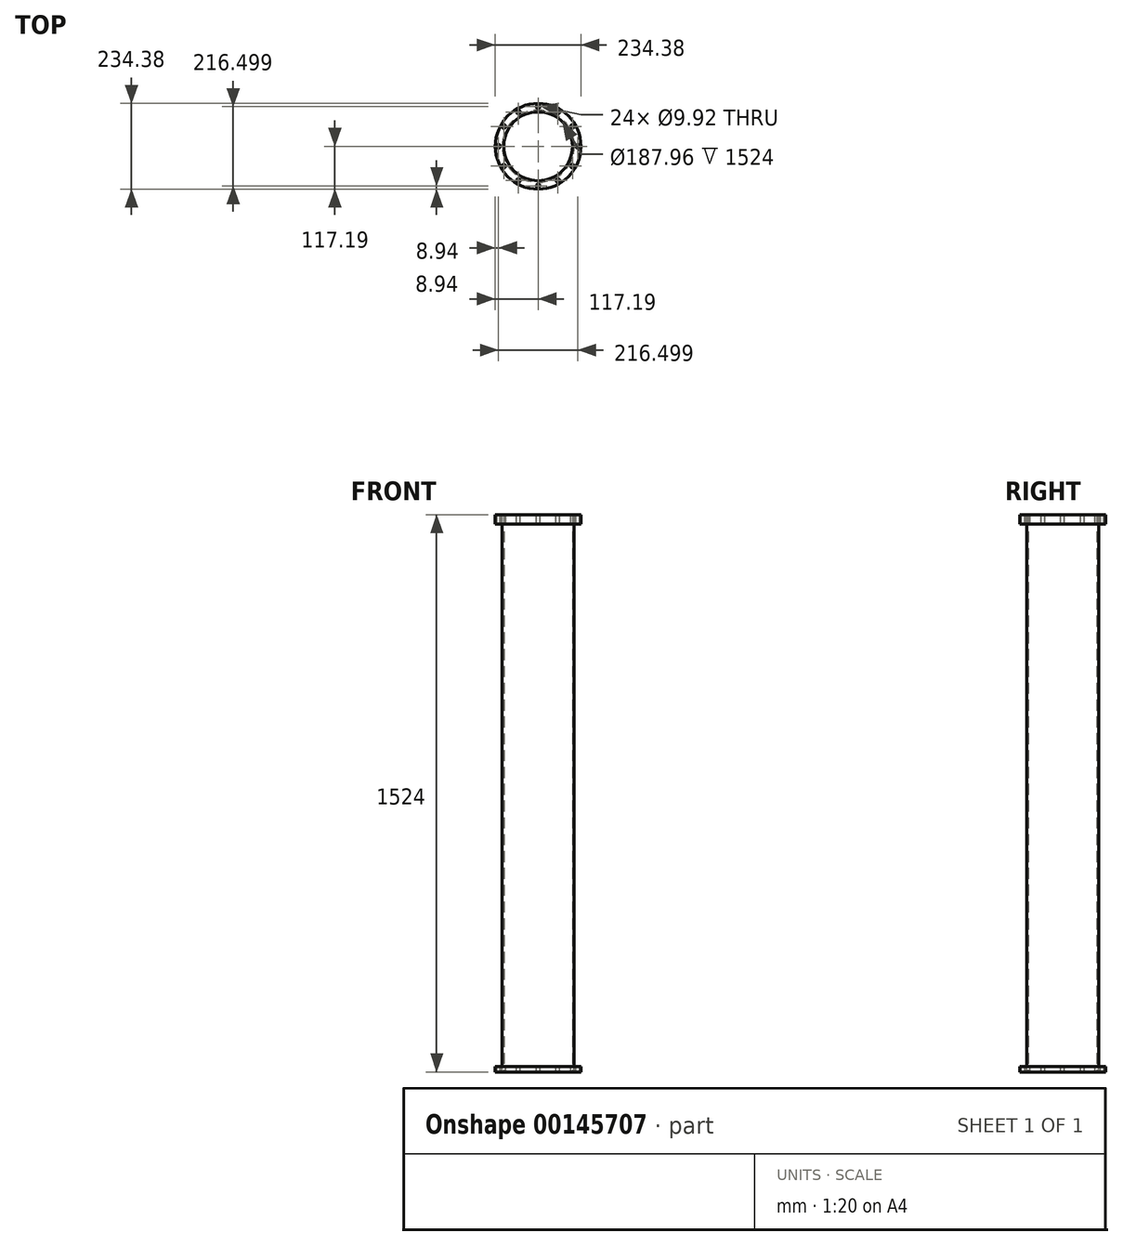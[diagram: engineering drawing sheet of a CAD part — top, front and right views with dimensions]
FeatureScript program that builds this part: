
annotation { "Feature Type Name" : "Feature", "Feature Type Description" : "" }
export const myFeature = defineFeature(function(context is Context, id is Id, definition is map)
    precondition{}
    {
        {
            var Q0;
            Q0=qCreatedBy(makeId("Top.planeOp"),FACE);
            var sketch = newSketch(context, id + "F0", { "sketchPlane" : qUnion([Q0])});
            skCircle(sketch, "E0", {"center": v(0, 0) * mm, "radius": 117.19 * mm});
            skCircle(sketch, "E1", {"center": v(0, 0) * mm, "radius": 98.47 * mm});
            skSolve(sketch);
        }
        {
            var Q0;
            Q0 = qSketchRegion(id + "F0", true);
            extrude(context, id + "F1", {"entities" : qUnion([Q0]), "depth" : 14.12 * mm});
        }
        {
            var Q0;
            Q0=makeQuery(id+"F1.opExtrude","CAP_FACE",FACE,{"disambiguationData":[OSD([sQuery(id+"F0.wireOp",EDGE,"E0"),sQuery(id+"F0.wireOp",EDGE,"E1")])],"isStart":true});
            var sketch = newSketch(context, id + "F2", { "sketchPlane" : qUnion([Q0])});
            skCircle(sketch, "E2", {"center": v(0, 0) * mm, "radius": 98.49 * mm});
            skCircle(sketch, "E3", {"center": v(0, 0) * mm, "radius": 93.98 * mm});
            skSolve(sketch);
        }
        {
            var Q0;
            Q0 = qSketchRegion(id + "F2", true);
            extrude(context, id + "F3", {"entities" : qUnion([Q0]), "operationType" : NewBodyOperationType.ADD, "oppositeDirection" : true, "depth" : 1524 * mm});
        }
        {
            var Q0;
            Q0=makeQuery(id+"F3.opExtrude","CAP_FACE",FACE,{"disambiguationData":[OSD([sQuery(id+"F2.wireOp",EDGE,"E2"),sQuery(id+"F2.wireOp",EDGE,"E3")])],"isStart":false});
            var sketch = newSketch(context, id + "F4", { "sketchPlane" : qUnion([Q0])});
            skCircle(sketch, "E4", {"center": v(0, 0) * mm, "radius": 98.47 * mm});
            skCircle(sketch, "E5", {"center": v(0, 0) * mm, "radius": 117.19 * mm});
            skSolve(sketch);
        }
        {
            var Q0;
            Q0 = qSketchRegion(id + "F4", true);
            extrude(context, id + "F5", {"entities" : qUnion([Q0]), "operationType" : NewBodyOperationType.ADD, "oppositeDirection" : true, "depth" : 25.4 * mm});
        }
        {
            var Q0;
            Q0=makeQuery(id+"F5.boolean.opBoolean","MERGE",FACE,{"derivedFrom":[makeQuery(id+"F3.opExtrude","CAP_FACE",FACE,{"disambiguationData":[OSD([sQuery(id+"F2.wireOp",EDGE,"E2"),sQuery(id+"F2.wireOp",EDGE,"E3")])],"isStart":false}),makeQuery(id+"F5.opExtrude","CAP_FACE",FACE,{"disambiguationData":[OSD([sQuery(id+"F4.wireOp",EDGE,"E4"),sQuery(id+"F4.wireOp",EDGE,"E5")])],"isStart":true})]});
            var sketch = newSketch(context, id + "F6", { "sketchPlane" : qUnion([Q0])});
            skCircle(sketch, "E6", {"center": v(0, -108.25) * mm, "radius": 4.96 * mm});
            skCircle(sketch, "E7.1.0", {"center": v(54.12, -93.75) * mm, "radius": 4.96 * mm});
            skCircle(sketch, "E7.2.0", {"center": v(93.75, -54.12) * mm, "radius": 4.96 * mm});
            skCircle(sketch, "E7.3.0", {"center": v(108.25, 0) * mm, "radius": 4.96 * mm});
            skCircle(sketch, "E7.4.0", {"center": v(93.75, 54.12) * mm, "radius": 4.96 * mm});
            skCircle(sketch, "E7.5.0", {"center": v(54.12, 93.75) * mm, "radius": 4.96 * mm});
            skCircle(sketch, "E7.6.0", {"center": v(0, 108.25) * mm, "radius": 4.96 * mm});
            skCircle(sketch, "E7.7.0", {"center": v(-54.12, 93.75) * mm, "radius": 4.96 * mm});
            skCircle(sketch, "E7.8.0", {"center": v(-93.75, 54.12) * mm, "radius": 4.96 * mm});
            skCircle(sketch, "E7.9.0", {"center": v(-108.25, 0) * mm, "radius": 4.96 * mm});
            skCircle(sketch, "E7.10.0", {"center": v(-93.75, -54.12) * mm, "radius": 4.96 * mm});
            skCircle(sketch, "E7.11.0", {"center": v(-54.12, -93.75) * mm, "radius": 4.96 * mm});
            skPoint(sketch, "E7.center", {"position": v(0, 0) * mm});
            skSolve(sketch);
        }
        {
            var Q0;
            Q0 = qSketchRegion(id + "F6", true);
            extrude(context, id + "F7", {"entities" : qUnion([Q0]), "operationType" : NewBodyOperationType.REMOVE, "endBound" : BoundingType.THROUGH_ALL, "oppositeDirection" : true, "depth" : 25.4 * mm});
        }
    });
